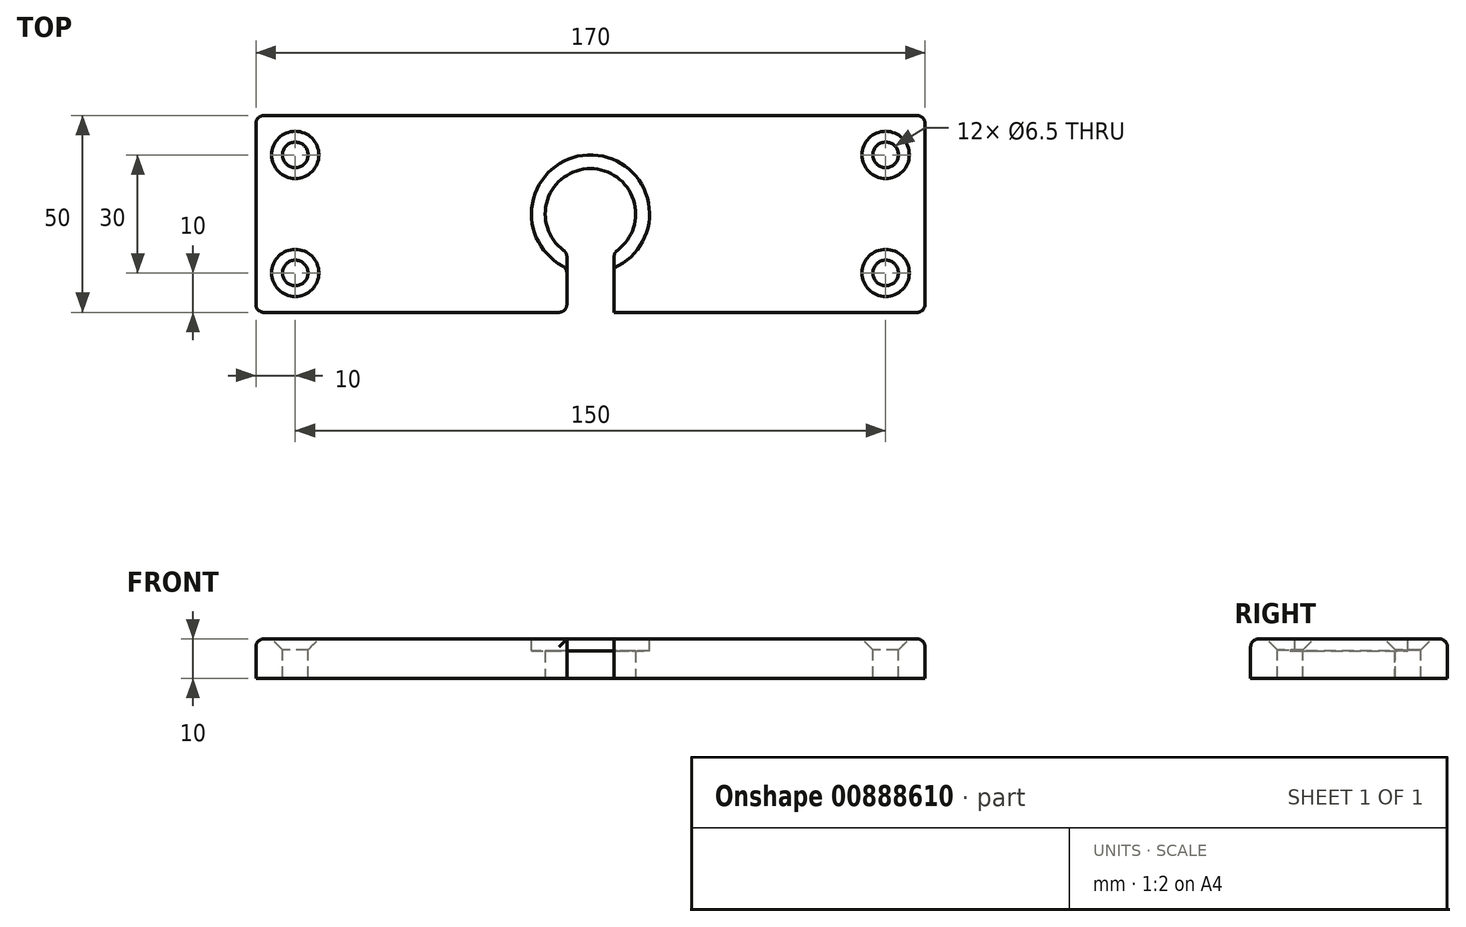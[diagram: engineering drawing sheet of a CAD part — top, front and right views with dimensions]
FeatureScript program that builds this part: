
annotation { "Feature Type Name" : "Feature", "Feature Type Description" : "" }
export const myFeature = defineFeature(function(context is Context, id is Id, definition is map)
    precondition{}
    {
        {
            var Q0;
            Q0=qCreatedBy(makeId("Top.planeOp"),FACE);
            var sketch = newSketch(context, id + "F0", { "sketchPlane" : qUnion([Q0])});
            skLineSegment(sketch, "E0.bottom", {"start": v(85, 25) * mm, "end": v(-85, 25) * mm});
            skLineSegment(sketch, "E0.top", {"start": v(85, -25) * mm, "end": v(-85, -25) * mm});
            skLineSegment(sketch, "E0.left", {"start": v(85, 25) * mm, "end": v(85, -25) * mm});
            skLineSegment(sketch, "E0.right", {"start": v(-85, 25) * mm, "end": v(-85, -25) * mm});
            skPoint(sketch, "E0.middle", {"position": v(0, 0) * mm});
            skCircle(sketch, "E1", {"center": v(0, 0) * mm, "radius": 11.5 * mm});
            skSolve(sketch);
        }
        {
            var Q0;
            Q0=makeQuery(id+"F0.imprint","IMPRINT",FACE,{"disambiguationData":[TD([[makeQuery(id+"F0.imprint","IMPRINT",EDGE,{"derivedFrom":sQuery(id+"F0.wireOp",EDGE,"E0.bottom")}),1.0]])]});
            extrude(context, id + "F1", {"entities" : qUnion([Q0]), "depth" : 10 * mm, "offsetDistance" : 25 * mm});
        }
        {
            var Q0;
            Q0=makeQuery(id+"F1.opExtrude","CAP_FACE",FACE,{"disambiguationData":[OSD([sQuery(id+"F0.wireOp",EDGE,"E0.bottom"),sQuery(id+"F0.wireOp",EDGE,"E0.top"),sQuery(id+"F0.wireOp",EDGE,"E0.left"),sQuery(id+"F0.wireOp",EDGE,"E0.right")])],"isStart":false});
            var sketch = newSketch(context, id + "F2", { "sketchPlane" : qUnion([Q0])});
            skLineSegment(sketch, "E2", {"start": v(-75, 25) * mm, "end": v(-75, -25) * mm, "construction": true});
            skCircle(sketch, "E3", {"center": v(-75, 15) * mm, "radius": 3.25 * mm});
            skCircle(sketch, "E4", {"center": v(-75, -15) * mm, "radius": 3.25 * mm});
            skCircle(sketch, "E5.MirrorC", {"center": v(75, -15) * mm, "radius": 3.25 * mm});
            skCircle(sketch, "E6.MirrorC", {"center": v(75, 15) * mm, "radius": 3.25 * mm});
            skLineSegment(sketch, "E7.MirrorCS", {"start": v(75, 25) * mm, "end": v(75, -25) * mm, "construction": true});
            skSolve(sketch);
        }
        {
            var Q0;
            Q0 = qSketchRegion(id + "F2", true);
            extrude(context, id + "F3", {"entities" : qUnion([Q0]), "operationType" : NewBodyOperationType.REMOVE, "endBound" : BoundingType.THROUGH_ALL, "oppositeDirection" : true, "depth" : 25 * mm, "offsetDistance" : 25 * mm});
        }
        {
            var Q0;
            Q0=makeQuery(id+"F1.opExtrude","CAP_FACE",FACE,{"disambiguationData":[OSD([sQuery(id+"F0.wireOp",EDGE,"E0.bottom"),sQuery(id+"F0.wireOp",EDGE,"E0.top"),sQuery(id+"F0.wireOp",EDGE,"E0.left"),sQuery(id+"F0.wireOp",EDGE,"E0.right"),sQuery(id+"F0.wireOp",EDGE,"E1")])],"isStart":false});
            var sketch = newSketch(context, id + "F4", { "sketchPlane" : qUnion([Q0])});
            skCircle(sketch, "E8", {"center": v(0, 0) * mm, "radius": 15 * mm});
            skSolve(sketch);
        }
        {
            var Q0;
            Q0=makeQuery(id+"F4.imprint","IMPRINT",FACE,{"disambiguationData":[TD([[makeQuery(id+"F4.imprint","IMPRINT",EDGE,{"derivedFrom":sQuery(id+"F4.wireOp",EDGE,"E8")}),1.0]])]});
            extrude(context, id + "F5", {"entities" : qUnion([Q0]), "operationType" : NewBodyOperationType.REMOVE, "oppositeDirection" : true, "depth" : 3 * mm, "offsetDistance" : 25 * mm});
        }
        {
            var Q0;
            Q0=makeQuery(id+"F1.opExtrude","CAP_FACE",FACE,{"disambiguationData":[OSD([sQuery(id+"F0.wireOp",EDGE,"E0.bottom"),sQuery(id+"F0.wireOp",EDGE,"E0.top"),sQuery(id+"F0.wireOp",EDGE,"E0.left"),sQuery(id+"F0.wireOp",EDGE,"E0.right"),sQuery(id+"F0.wireOp",EDGE,"E1")])],"isStart":false});
            var sketch = newSketch(context, id + "F6", { "sketchPlane" : qUnion([Q0])});
            skLineSegment(sketch, "E9.bottom", {"start": v(-6, -25) * mm, "end": v(6, -25) * mm});
            skLineSegment(sketch, "E9.top", {"start": v(-6, -9) * mm, "end": v(6, -9) * mm});
            skLineSegment(sketch, "E9.left", {"start": v(-6, -25) * mm, "end": v(-6, -9) * mm});
            skLineSegment(sketch, "E9.right", {"start": v(6, -25) * mm, "end": v(6, -9) * mm});
            skSolve(sketch);
        }
        {
            var Q0;
            {var subQ0=sQuery(id+"F6.wireOp",EDGE,"E9.bottom");Q0=makeQuery(id+"F6.imprint","IMPRINT",FACE,{"disambiguationData":[TD([[makeQuery(id+"F6.imprint","IMPRINT",EDGE,{"derivedFrom":subQ0}),-1.0]])]});}
            var Q1;
            {var subQ0=sQuery(id+"F6.wireOp",EDGE,"E9.top");Q1=makeQuery(id+"F6.imprint","IMPRINT",FACE,{"disambiguationData":[TD([[makeQuery(id+"F6.imprint","IMPRINT",EDGE,{"derivedFrom":subQ0}),-1.0]])]});}
            extrude(context, id + "F7", {"entities" : qUnion([Q0, Q1]), "operationType" : NewBodyOperationType.REMOVE, "oppositeDirection" : true, "depth" : 25 * mm, "offsetDistance" : 25 * mm});
        }
        {
            var Q0;
            Q0=makeQuery(id+"F7.boolean.opBoolean","COPY",EDGE,{"derivedFrom":makeQuery(id+"F7.opExtrude","SWEPT_EDGE",EDGE,{"disambiguationData":[OSD([sQuery(id+"F0.wireOp",EDGE,"E0.top"),sQuery(id+"F6.wireOp",EDGE,"E9.bottom"),sQuery(id+"F6.wireOp",EDGE,"E9.left")])]})});
            var Q1;
            Q1=makeQuery(id+"F7.boolean.opBoolean","COPY",EDGE,{"derivedFrom":makeQuery(id+"F7.opExtrude","SWEPT_EDGE",EDGE,{"disambiguationData":[OSD([sQuery(id+"F0.wireOp",EDGE,"E0.top"),sQuery(id+"F6.wireOp",EDGE,"E9.bottom"),sQuery(id+"F6.wireOp",EDGE,"E9.right")])]})});
            var Q2;
            Q2=makeQuery(id+"F7.boolean.opBoolean","INTERSECT",EDGE,{"derivedFrom":[makeQuery(id+"F1.opExtrude","SWEPT_FACE",FACE,{"disambiguationData":[OSD([sQuery(id+"F0.wireOp",EDGE,"E1")])]}),makeQuery(id+"F7.opExtrude","SWEPT_FACE",FACE,{"disambiguationData":[OSD([sQuery(id+"F6.wireOp",EDGE,"E9.left")])]})]});
            var Q3;
            Q3=makeQuery(id+"F7.boolean.opBoolean","INTERSECT",EDGE,{"derivedFrom":[makeQuery(id+"F1.opExtrude","SWEPT_FACE",FACE,{"disambiguationData":[OSD([sQuery(id+"F0.wireOp",EDGE,"E1")])]}),makeQuery(id+"F7.opExtrude","SWEPT_FACE",FACE,{"disambiguationData":[OSD([sQuery(id+"F6.wireOp",EDGE,"E9.right")])]})]});
            var Q4;
            Q4=makeQuery(id+"F7.boolean.opBoolean","INTERSECT",EDGE,{"derivedFrom":[makeQuery(id+"F5.boolean.opBoolean","COPY",FACE,{"derivedFrom":makeQuery(id+"F5.opExtrude","SWEPT_FACE",FACE,{"disambiguationData":[OSD([sQuery(id+"F4.wireOp",EDGE,"E8")])]})}),makeQuery(id+"F7.opExtrude","SWEPT_FACE",FACE,{"disambiguationData":[OSD([sQuery(id+"F6.wireOp",EDGE,"E9.left")])]})]});
            fillet(context, id + "F8", {"entities" : qUnion([Q0, Q1, Q2, Q3, Q4]), "radius" : 2 * mm, "tangentPropagation" : true, "allowEdgeOverflow" : false});
        }
        {
            var Q0;
            Q0=makeQuery(id+"F1.opExtrude","CAP_EDGE",EDGE,{"disambiguationData":[OSD([sQuery(id+"F0.wireOp",EDGE,"E0.right")])],"isStart":false});
            var Q1;
            Q1=makeQuery(id+"F1.opExtrude","CAP_EDGE",EDGE,{"disambiguationData":[OSD([sQuery(id+"F0.wireOp",EDGE,"E0.bottom")])],"isStart":false});
            var Q2;
            Q2=makeQuery(id+"F1.opExtrude","CAP_EDGE",EDGE,{"disambiguationData":[OSD([sQuery(id+"F0.wireOp",EDGE,"E0.left")])],"isStart":false});
            var Q3;
            Q3=makeQuery(id+"F1.opExtrude","SWEPT_EDGE",EDGE,{"disambiguationData":[OSD([sQuery(id+"F0.wireOp",EDGE,"E0.top"),sQuery(id+"F0.wireOp",EDGE,"E0.left")])]});
            var Q4;
            Q4=makeQuery(id+"F1.opExtrude","SWEPT_EDGE",EDGE,{"disambiguationData":[OSD([sQuery(id+"F0.wireOp",EDGE,"E0.bottom"),sQuery(id+"F0.wireOp",EDGE,"E0.left")])]});
            var Q5;
            Q5=makeQuery(id+"F1.opExtrude","SWEPT_EDGE",EDGE,{"disambiguationData":[OSD([sQuery(id+"F0.wireOp",EDGE,"E0.top"),sQuery(id+"F0.wireOp",EDGE,"E0.right")])]});
            var Q6;
            Q6=makeQuery(id+"F1.opExtrude","SWEPT_EDGE",EDGE,{"disambiguationData":[OSD([sQuery(id+"F0.wireOp",EDGE,"E0.bottom"),sQuery(id+"F0.wireOp",EDGE,"E0.right")])]});
            var Q7;
            {var subQ0=sQuery(id+"F0.wireOp",EDGE,"E0.left");var subQ1=sQuery(id+"F0.wireOp",EDGE,"E0.top");Q7=makeQuery(id+"F7.boolean.opBoolean","SPLIT",EDGE,{"disambiguationData":[TD([makeQuery(id+"F1.opExtrude","SWEPT_FACE",FACE,{"disambiguationData":[OSD([subQ0])]})])],"derivedFrom":makeQuery(id+"F1.opExtrude","CAP_EDGE",EDGE,{"disambiguationData":[OSD([subQ1])],"isStart":false})});}
            var Q8;
            {var subQ0=sQuery(id+"F0.wireOp",EDGE,"E0.right");var subQ1=sQuery(id+"F0.wireOp",EDGE,"E0.top");Q8=makeQuery(id+"F7.boolean.opBoolean","SPLIT",EDGE,{"disambiguationData":[TD([makeQuery(id+"F1.opExtrude","SWEPT_FACE",FACE,{"disambiguationData":[OSD([subQ0])]})])],"derivedFrom":makeQuery(id+"F1.opExtrude","CAP_EDGE",EDGE,{"disambiguationData":[OSD([subQ1])],"isStart":false})});}
            fillet(context, id + "F9", {"entities" : qUnion([Q0, Q1, Q2, Q3, Q4, Q5, Q6, Q7, Q8]), "radius" : 2 * mm, "allowEdgeOverflow" : false});
        }
        {
            var Q0;
            Q0=makeQuery(id+"F1.opExtrude","CAP_FACE",FACE,{"disambiguationData":[OSD([sQuery(id+"F0.wireOp",EDGE,"E0.bottom"),sQuery(id+"F0.wireOp",EDGE,"E0.top"),sQuery(id+"F0.wireOp",EDGE,"E0.left"),sQuery(id+"F0.wireOp",EDGE,"E0.right"),sQuery(id+"F0.wireOp",EDGE,"E1")])],"isStart":false});
            var sketch = newSketch(context, id + "F10", { "sketchPlane" : qUnion([Q0])});
            skCircle(sketch, "E10", {"center": v(-75, 15) * mm, "radius": 3 * mm});
            skCircle(sketch, "E11", {"center": v(-75, -15) * mm, "radius": 3 * mm});
            skCircle(sketch, "E12", {"center": v(75, 15) * mm, "radius": 3 * mm});
            skCircle(sketch, "E13", {"center": v(75, -15) * mm, "radius": 3 * mm});
            skSolve(sketch);
        }
        {
            var Q0;
            Q0=sQuery(id+"F10.wireOp",VERTEX,"E10.center");
            var Q1;
            Q1=sQuery(id+"F10.wireOp",VERTEX,"E11.center");
            var Q2;
            Q2=sQuery(id+"F10.wireOp",VERTEX,"E13.center");
            var Q3;
            Q3=sQuery(id+"F10.wireOp",VERTEX,"E12.center");
            var Q4;
            Q4=makeQuery(id+"F1.opExtrude","SWEPT_BODY",BODY,{"disambiguationData":[OSD([sQuery(id+"F0.wireOp",EDGE,"E0.bottom"),sQuery(id+"F0.wireOp",EDGE,"E0.top"),sQuery(id+"F0.wireOp",EDGE,"E0.left"),sQuery(id+"F0.wireOp",EDGE,"E0.right"),sQuery(id+"F0.wireOp",EDGE,"E1")])]});
            hole(context, id + "F11", {"style" : HoleStyle.C_SINK, "endStyle" : HoleEndStyle.BLIND, "holeDiameter" : 6.5 * mm, "cSinkDiameter" : 12 * mm, "cSinkAngle" : 90 * degree, "majorDiameter" : 5 * mm, "holeDepth" : 15 * mm, "tappedDepth" : 17.6 * mm, "tapClearance" : 3, "locations" : qUnion([Q0, Q1, Q2, Q3]), "scope" : qUnion([Q4])});
        }
    });
